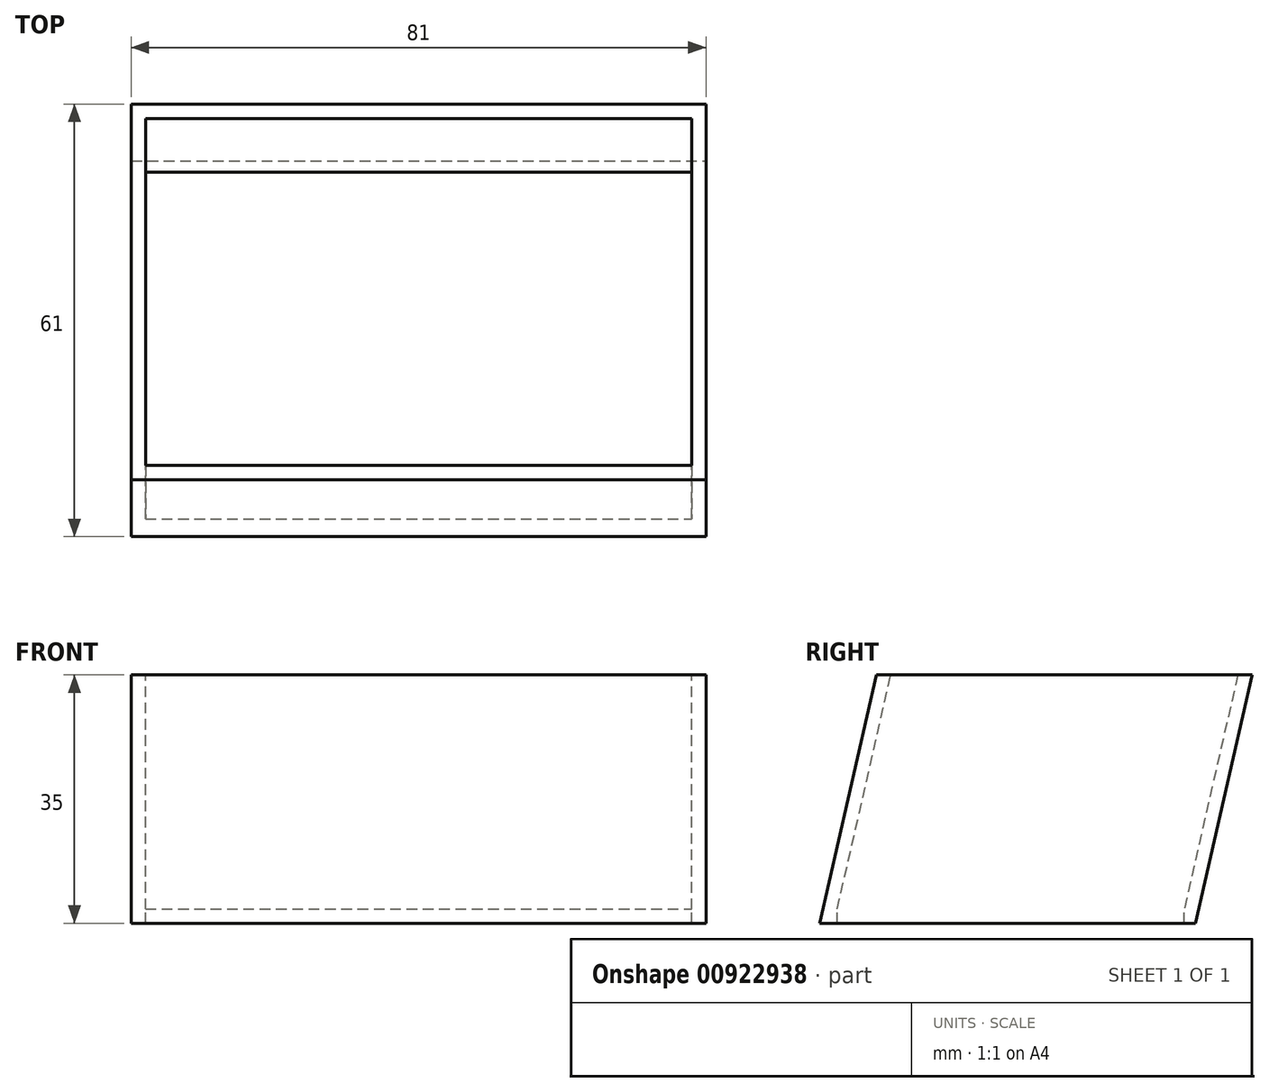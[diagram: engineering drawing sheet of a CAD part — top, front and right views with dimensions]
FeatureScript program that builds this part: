
annotation { "Feature Type Name" : "Feature", "Feature Type Description" : "" }
export const myFeature = defineFeature(function(context is Context, id is Id, definition is map)
    precondition{}
    {
        {
            var Q0;
            Q0=qCreatedBy(makeId("Top.planeOp"),FACE);
            var sketch = newSketch(context, id + "F0", { "sketchPlane" : qUnion([Q0])});
            skLineSegment(sketch, "E0.bottom", {"start": v(-33.96, 26.5) * mm, "end": v(47.04, 26.5) * mm});
            skLineSegment(sketch, "E0.top", {"start": v(-33.96, -26.5) * mm, "end": v(47.04, -26.5) * mm});
            skLineSegment(sketch, "E0.left", {"start": v(-33.96, 26.5) * mm, "end": v(-33.96, -26.5) * mm});
            skLineSegment(sketch, "E0.right", {"start": v(47.04, 26.5) * mm, "end": v(47.04, -26.5) * mm});
            skPoint(sketch, "E0.middle", {"position": v(6.54, 0) * mm});
            skSolve(sketch);
        }
        {
            var Q0;
            Q0=makeQuery(id+"F0.imprint","IMPRINT",FACE,{"disambiguationData":[TD([[makeQuery(id+"F0.imprint","IMPRINT",EDGE,{"derivedFrom":sQuery(id+"F0.wireOp",EDGE,"E0.bottom")}),-1.0]])]});
            extrude(context, id + "F1", {"entities" : qUnion([Q0]), "depth" : 35 * mm, "offsetDistance" : 25 * mm});
        }
        {
            var Q0;
            Q0=makeQuery(id+"F1.opExtrude","SWEPT_FACE",FACE,{"disambiguationData":[OSD([sQuery(id+"F0.wireOp",EDGE,"E0.right")])]});
            var sketch = newSketch(context, id + "F2", { "sketchPlane" : qUnion([Q0])});
            skLineSegment(sketch, "E1", {"start": v(-26.5, 0) * mm, "end": v(-18.5, 35) * mm});
            skLineSegment(sketch, "E2", {"start": v(26.5, 0) * mm, "end": v(34.5, 35) * mm});
            skLineSegment(sketch, "E3", {"start": v(34.5, 35) * mm, "end": v(26.5, 35) * mm});
            skSolve(sketch);
        }
        {
            var Q0;
            Q0=makeQuery(id+"F2.imprint","IMPRINT",FACE,{"disambiguationData":[TD([[makeQuery(id+"F2.imprint","IMPRINT",EDGE,{"derivedFrom":sQuery(id+"F2.wireOp",EDGE,"E2")}),1.0]])]});
            var Q1;
            Q1=makeQuery(id+"F1.opExtrude","SWEPT_FACE",FACE,{"disambiguationData":[OSD([sQuery(id+"F0.wireOp",EDGE,"E0.left")])]});
            extrude(context, id + "F3", {"entities" : qUnion([Q0]), "operationType" : NewBodyOperationType.ADD, "endBound" : BoundingType.UP_TO_SURFACE, "oppositeDirection" : true, "depth" : 25 * mm, "endBoundEntityFace" : qUnion([Q1]), "offsetDistance" : 25 * mm});
        }
        {
            var Q0;
            {var subQ0=sQuery(id+"F2.wireOp",EDGE,"E1");Q0=makeQuery(id+"F2.imprint","IMPRINT",FACE,{"disambiguationData":[TD([[makeQuery(id+"F2.imprint","IMPRINT",EDGE,{"derivedFrom":subQ0}),1.0]])]});}
            extrude(context, id + "F4", {"entities" : qUnion([Q0]), "operationType" : NewBodyOperationType.REMOVE, "endBound" : BoundingType.THROUGH_ALL, "oppositeDirection" : true, "depth" : 25 * mm, "offsetDistance" : 25 * mm});
        }
        {
            var Q0;
            Q0=makeQuery(id+"F3.boolean.opBoolean","MERGE",FACE,{"derivedFrom":[makeQuery(id+"F1.opExtrude","CAP_FACE",FACE,{"disambiguationData":[OSD([sQuery(id+"F0.wireOp",EDGE,"E0.bottom"),sQuery(id+"F0.wireOp",EDGE,"E0.top"),sQuery(id+"F0.wireOp",EDGE,"E0.left"),sQuery(id+"F0.wireOp",EDGE,"E0.right")])],"isStart":false}),makeQuery(id+"F3.opExtrude","SWEPT_FACE",FACE,{"disambiguationData":[OSD([sQuery(id+"F2.wireOp",EDGE,"E3")])]})]});
            shell(context, id + "F5", {"entities" : qUnion([Q0]), "thickness" : 2 * mm});
        }
        {
            var Q0;
            Q0=makeQuery(id+"F5.opShell","OFFSET_FACE",FACE,{"disambiguationData":[OSD([sQuery(id+"F0.wireOp",EDGE,"E0.bottom"),sQuery(id+"F0.wireOp",EDGE,"E0.top"),sQuery(id+"F0.wireOp",EDGE,"E0.left"),sQuery(id+"F0.wireOp",EDGE,"E0.right")])]});
            extrude(context, id + "F6", {"entities" : qUnion([Q0]), "operationType" : NewBodyOperationType.REMOVE, "oppositeDirection" : true, "depth" : 25 * mm, "offsetDistance" : 25 * mm});
        }
    });
